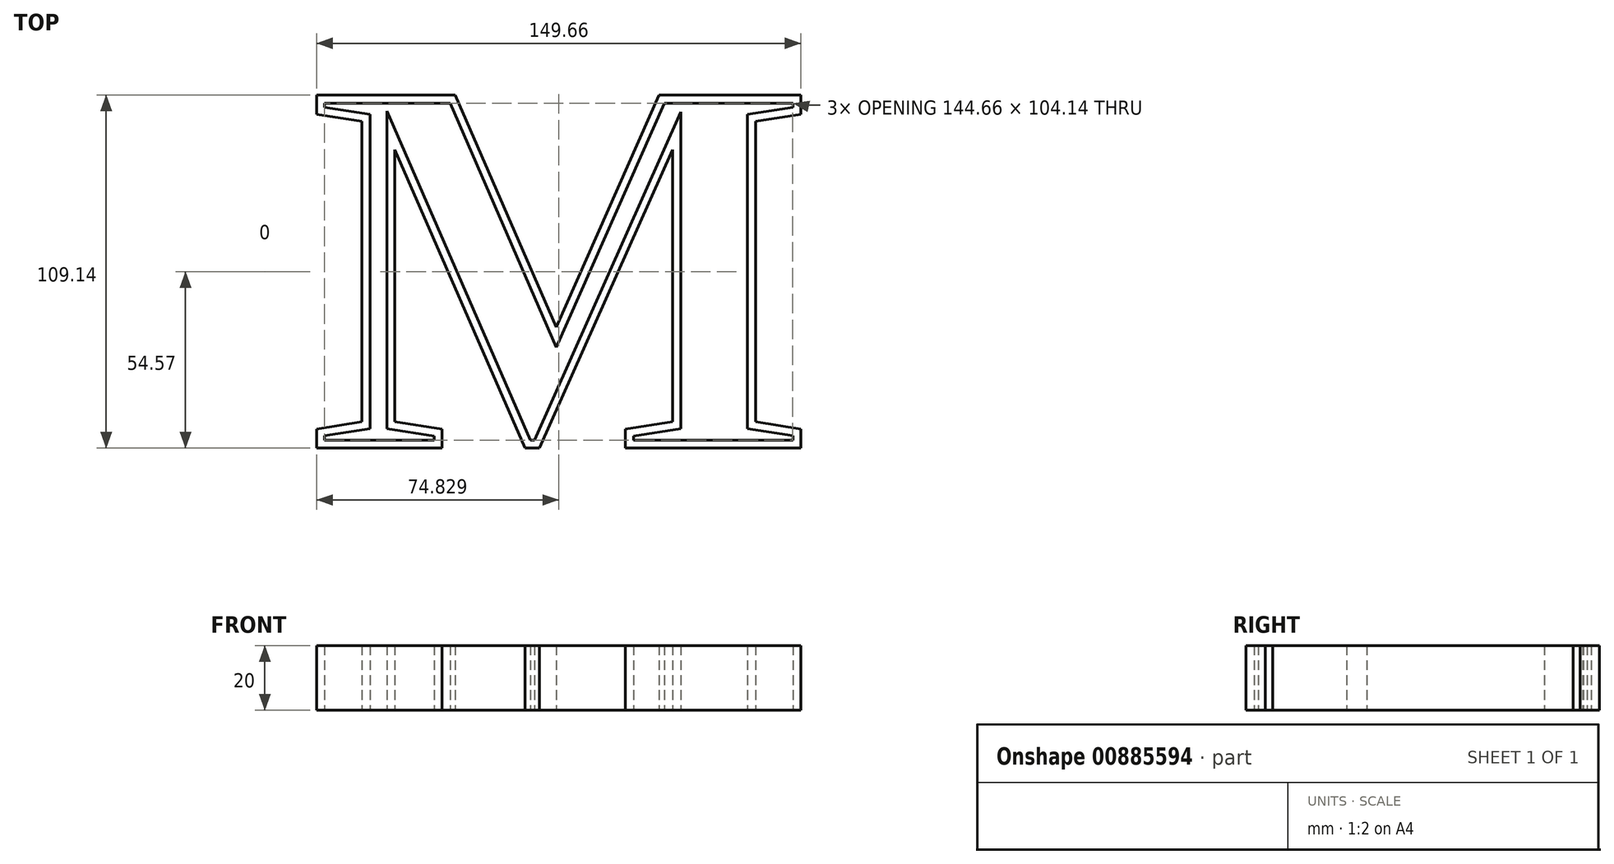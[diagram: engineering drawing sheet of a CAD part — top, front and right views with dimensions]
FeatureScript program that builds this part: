
annotation { "Feature Type Name" : "Feature", "Feature Type Description" : "" }
export const myFeature = defineFeature(function(context is Context, id is Id, definition is map)
    precondition{}
    {
        {
            var Q0;
            Q0=qCreatedBy(makeId("Top.planeOp"),FACE);
            var sketch = newSketch(context, id + "F0", { "sketchPlane" : qUnion([Q0])});
            skText(sketch, "E0", { "text": "M", "fontName": "Tinos-Bold.ttf"});
            skPoint(sketch, "E1", {"position": v(0, 0) * mm});
            const initialGuessF0  = {"E0": [-0.08146, -0.06, 1, 0, 0.12]};
            skSetInitialGuess(sketch, initialGuessF0);
            skSolve(sketch);
        }
        {
            var Q0;
            Q0=makeQuery(id+"F0.imprint","IMPRINT",FACE,{"disambiguationData":[TD([[makeQuery(id+"F0.imprint","IMPRINT",EDGE,{"derivedFrom":sQuery(id+"F0.wireOp",EDGE,"E0.sketch_text.stroke-0")}),-1.0]])]});
            extrude(context, id + "F1", {"entities" : qUnion([Q0]), "depth" : 20 * mm, "offsetDistance" : 25 * mm});
        }
        {
            var Q0;
            Q0=makeQuery(id+"F1.opExtrude","CAP_FACE",FACE,{"disambiguationData":[OSD([sQuery(id+"F0.wireOp",EDGE,"E0.sketch_text.stroke-0"),sQuery(id+"F0.wireOp",EDGE,"E0.sketch_text.stroke-1"),sQuery(id+"F0.wireOp",EDGE,"E0.sketch_text.stroke-2"),sQuery(id+"F0.wireOp",EDGE,"E0.sketch_text.stroke-3"),sQuery(id+"F0.wireOp",EDGE,"E0.sketch_text.stroke-4"),sQuery(id+"F0.wireOp",EDGE,"E0.sketch_text.stroke-5"),sQuery(id+"F0.wireOp",EDGE,"E0.sketch_text.stroke-6"),sQuery(id+"F0.wireOp",EDGE,"E0.sketch_text.stroke-7"),sQuery(id+"F0.wireOp",EDGE,"E0.sketch_text.stroke-8"),sQuery(id+"F0.wireOp",EDGE,"E0.sketch_text.stroke-9"),sQuery(id+"F0.wireOp",EDGE,"E0.sketch_text.stroke-10"),sQuery(id+"F0.wireOp",EDGE,"E0.sketch_text.stroke-11"),sQuery(id+"F0.wireOp",EDGE,"E0.sketch_text.stroke-12"),sQuery(id+"F0.wireOp",EDGE,"E0.sketch_text.stroke-13"),sQuery(id+"F0.wireOp",EDGE,"E0.sketch_text.stroke-14"),sQuery(id+"F0.wireOp",EDGE,"E0.sketch_text.stroke-15"),sQuery(id+"F0.wireOp",EDGE,"E0.sketch_text.stroke-16"),sQuery(id+"F0.wireOp",EDGE,"E0.sketch_text.stroke-17"),sQuery(id+"F0.wireOp",EDGE,"E0.sketch_text.stroke-18"),sQuery(id+"F0.wireOp",EDGE,"E0.sketch_text.stroke-19"),sQuery(id+"F0.wireOp",EDGE,"E0.sketch_text.stroke-20"),sQuery(id+"F0.wireOp",EDGE,"E0.sketch_text.stroke-21"),sQuery(id+"F0.wireOp",EDGE,"E0.sketch_text.stroke-22"),sQuery(id+"F0.wireOp",EDGE,"E0.sketch_text.stroke-23"),sQuery(id+"F0.wireOp",EDGE,"E0.sketch_text.stroke-24")])],"isStart":false});
            shell(context, id + "F2", {"entities" : qUnion([Q0]), "thickness" : 2.5 * mm});
        }
        {
            var Q0;
            Q0=makeQuery(id+"F2.opShell","OFFSET_FACE",FACE,{"disambiguationData":[OSD([sQuery(id+"F0.wireOp",EDGE,"E0.sketch_text.stroke-0"),sQuery(id+"F0.wireOp",EDGE,"E0.sketch_text.stroke-1"),sQuery(id+"F0.wireOp",EDGE,"E0.sketch_text.stroke-2"),sQuery(id+"F0.wireOp",EDGE,"E0.sketch_text.stroke-3"),sQuery(id+"F0.wireOp",EDGE,"E0.sketch_text.stroke-4"),sQuery(id+"F0.wireOp",EDGE,"E0.sketch_text.stroke-5"),sQuery(id+"F0.wireOp",EDGE,"E0.sketch_text.stroke-6"),sQuery(id+"F0.wireOp",EDGE,"E0.sketch_text.stroke-7"),sQuery(id+"F0.wireOp",EDGE,"E0.sketch_text.stroke-8"),sQuery(id+"F0.wireOp",EDGE,"E0.sketch_text.stroke-9"),sQuery(id+"F0.wireOp",EDGE,"E0.sketch_text.stroke-10"),sQuery(id+"F0.wireOp",EDGE,"E0.sketch_text.stroke-11"),sQuery(id+"F0.wireOp",EDGE,"E0.sketch_text.stroke-12"),sQuery(id+"F0.wireOp",EDGE,"E0.sketch_text.stroke-13"),sQuery(id+"F0.wireOp",EDGE,"E0.sketch_text.stroke-14"),sQuery(id+"F0.wireOp",EDGE,"E0.sketch_text.stroke-15"),sQuery(id+"F0.wireOp",EDGE,"E0.sketch_text.stroke-16"),sQuery(id+"F0.wireOp",EDGE,"E0.sketch_text.stroke-17"),sQuery(id+"F0.wireOp",EDGE,"E0.sketch_text.stroke-18"),sQuery(id+"F0.wireOp",EDGE,"E0.sketch_text.stroke-19"),sQuery(id+"F0.wireOp",EDGE,"E0.sketch_text.stroke-20"),sQuery(id+"F0.wireOp",EDGE,"E0.sketch_text.stroke-21"),sQuery(id+"F0.wireOp",EDGE,"E0.sketch_text.stroke-22"),sQuery(id+"F0.wireOp",EDGE,"E0.sketch_text.stroke-23"),sQuery(id+"F0.wireOp",EDGE,"E0.sketch_text.stroke-24")])]});
            extrude(context, id + "F3", {"entities" : qUnion([Q0]), "operationType" : NewBodyOperationType.REMOVE, "oppositeDirection" : true, "depth" : 25 * mm, "offsetDistance" : 25 * mm});
        }
    });
